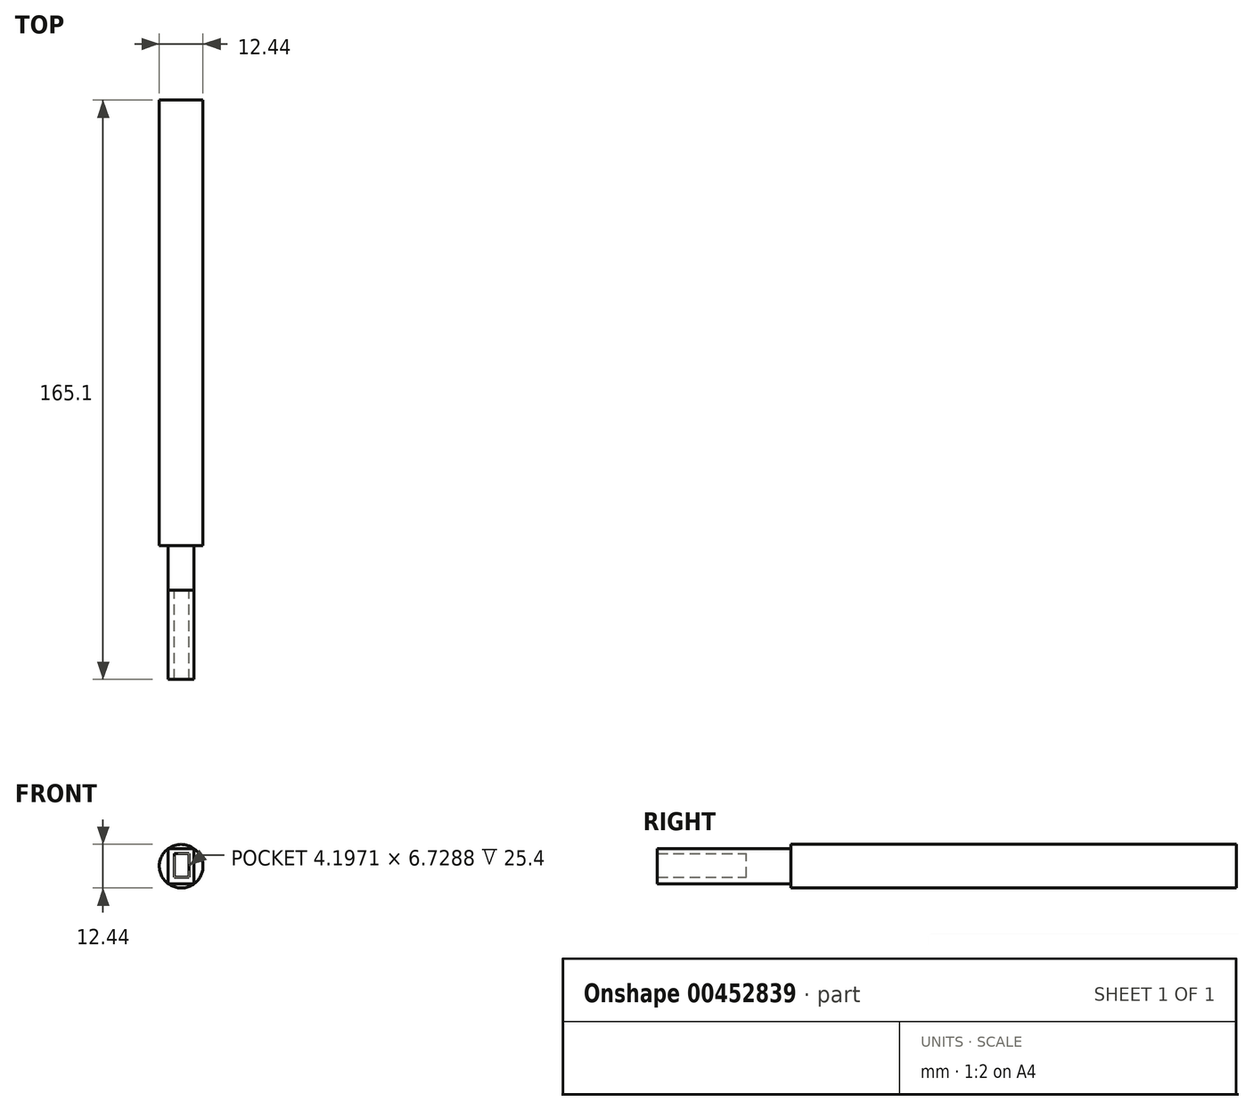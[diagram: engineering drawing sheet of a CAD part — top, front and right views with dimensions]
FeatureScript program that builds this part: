
annotation { "Feature Type Name" : "Feature", "Feature Type Description" : "" }
export const myFeature = defineFeature(function(context is Context, id is Id, definition is map)
    precondition{}
    {
        {
            var Q0;
            Q0=qCreatedBy(makeId("Front.planeOp"),FACE);
            var sketch = newSketch(context, id + "F0", { "sketchPlane" : qUnion([Q0])});
            skCircle(sketch, "E0", {"center": v(0, 0) * mm, "radius": 6.22 * mm});
            skSolve(sketch);
        }
        {
            var Q0;
            Q0 = qSketchRegion(id + "F0", true);
            extrude(context, id + "F1", {"entities" : qUnion([Q0]), "depth" : 127 * mm});
        }
        {
            var Q0;
            Q0=makeQuery(id+"F1.opExtrude","CAP_FACE",FACE,{"disambiguationData":[OSD([sQuery(id+"F0.wireOp",EDGE,"E0")])],"isStart":false});
            var sketch = newSketch(context, id + "F2", { "sketchPlane" : qUnion([Q0])});
            skLineSegment(sketch, "E1.bottom", {"start": v(0, -6.22) * mm, "end": v(0, -6.22) * mm});
            skLineSegment(sketch, "E1.top", {"start": v(0, 6.22) * mm, "end": v(0, 6.22) * mm});
            skLineSegment(sketch, "E2.bottom", {"start": v(3.69, -5.01) * mm, "end": v(-3.68, -5.01) * mm});
            skLineSegment(sketch, "E2.top", {"start": v(3.69, 5.02) * mm, "end": v(-3.68, 5.02) * mm});
            skLineSegment(sketch, "E2.left", {"start": v(3.69, -5.01) * mm, "end": v(3.69, 5.02) * mm});
            skLineSegment(sketch, "E2.right", {"start": v(-3.68, -5.01) * mm, "end": v(-3.68, 5.02) * mm});
            skSolve(sketch);
        }
        {
            var Q0;
            {var subQ1=sQuery(id+"F2.wireOp",EDGE,"E2.bottom");Q0=makeQuery(id+"F2.imprint","IMPRINT",FACE,{"disambiguationData":[TD([[makeQuery(id+"F2.imprint","IMPRINT",EDGE,{"derivedFrom":subQ1}),-1.0]])]});}
            extrude(context, id + "F3", {"entities" : qUnion([Q0]), "operationType" : NewBodyOperationType.ADD, "depth" : 12.7 * mm});
        }
        {
            var Q0;
            Q0=makeQuery(id+"F3.opExtrude","CAP_FACE",FACE,{"disambiguationData":[OSD([sQuery(id+"F0.wireOp",EDGE,"E0"),sQuery(id+"F2.wireOp",EDGE,"E2.bottom"),sQuery(id+"F2.wireOp",EDGE,"E2.top"),sQuery(id+"F2.wireOp",EDGE,"E2.left"),sQuery(id+"F2.wireOp",EDGE,"E2.right")])],"isStart":false});
            var sketch = newSketch(context, id + "F4", { "sketchPlane" : qUnion([Q0])});
            skLineSegment(sketch, "E3.bottom", {"start": v(-1.96, -3.15) * mm, "end": v(2.24, -3.15) * mm});
            skLineSegment(sketch, "E3.top", {"start": v(-1.96, 3.58) * mm, "end": v(2.24, 3.58) * mm});
            skLineSegment(sketch, "E3.left", {"start": v(-1.96, -3.15) * mm, "end": v(-1.96, 3.58) * mm});
            skLineSegment(sketch, "E3.right", {"start": v(2.24, -3.15) * mm, "end": v(2.24, 3.58) * mm});
            skLineSegment(sketch, "E4", {"start": v(-1.96, 3.58) * mm, "end": v(-3.68, 5.02) * mm});
            skLineSegment(sketch, "E5", {"start": v(2.24, 3.58) * mm, "end": v(3.69, 5.01) * mm});
            skLineSegment(sketch, "E6", {"start": v(2.24, -3.15) * mm, "end": v(3.69, -5.01) * mm});
            skLineSegment(sketch, "E7", {"start": v(-1.96, -3.15) * mm, "end": v(-3.68, -5.01) * mm});
            skLineSegment(sketch, "E8", {"start": v(-3.68, -5.01) * mm, "end": v(-3.68, 5.02) * mm});
            skLineSegment(sketch, "E9", {"start": v(-3.68, 5.02) * mm, "end": v(3.69, 5.01) * mm});
            skLineSegment(sketch, "E10", {"start": v(3.69, -5.01) * mm, "end": v(3.69, 5.01) * mm});
            skLineSegment(sketch, "E11", {"start": v(-3.68, -5.01) * mm, "end": v(3.69, -5.01) * mm});
            skSolve(sketch);
        }
        {
            var Q0;
            Q0 = qSketchRegion(id + "F4", true);
            extrude(context, id + "F5", {"entities" : qUnion([Q0]), "operationType" : NewBodyOperationType.ADD, "depth" : 25.4 * mm});
        }
    });
